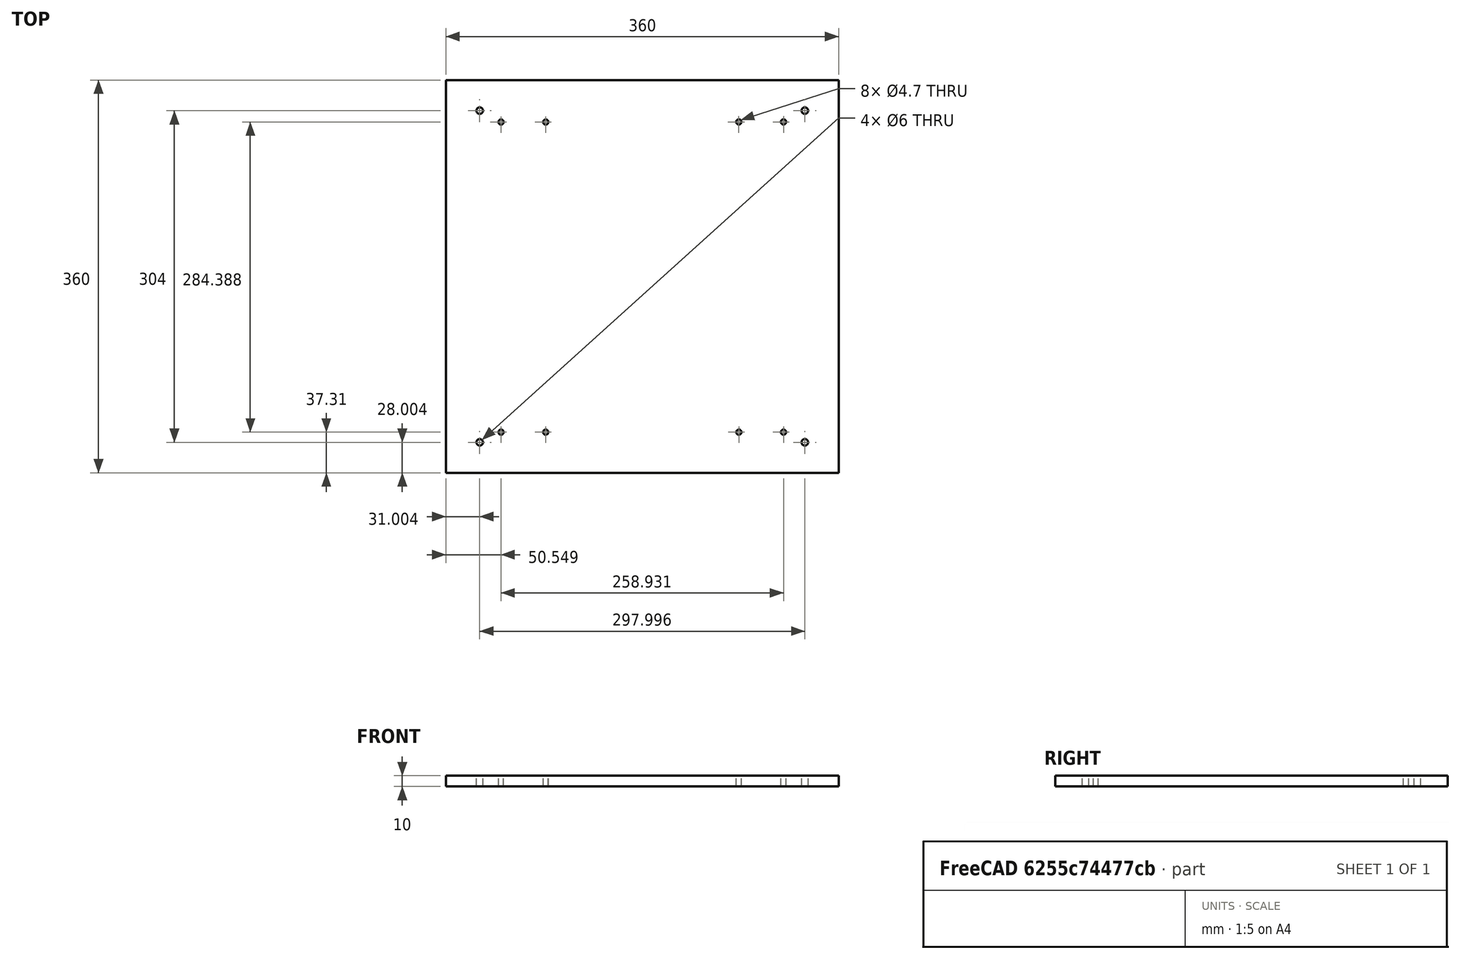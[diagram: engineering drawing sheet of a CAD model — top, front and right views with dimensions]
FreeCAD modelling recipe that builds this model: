
FCSTD DOCUMENT  (FreeCAD 0.14R3702 (Git))
Label: bed
License: CC-BY 3.0
LicenseURL: http://creativecommons.org/licenses/by/3.0/
objects: Part::Cylinder×12, Part::Cut×12, Part::Box×1
note: 25 computed .brp shape members not serialized (recipe doc carries the construction recipe); baked Part::Feature solids carry a one-line shape summary decoded from their .brp

FEATURE [Part::Box] Box  label="Cube"
  Height = 10
  Length = 360
  Placement = pos=(795.334,70.8936,98.54) rot=(0,0,1;0rad)
  Width = 360
FEATURE [Part::Cylinder] Cylinder
  Angle = 360
  Height = 100
  Placement = pos=(845.879,108.2,42.0127) rot=(0,0,1;0rad)
  Radius = 2.35
FEATURE [Part::Cylinder] Cylinder001
  Angle = 360
  Height = 100
  Placement = pos=(886.821,108.2,42.0127) rot=(0,0,1;0rad)
  Radius = 2.35
FEATURE [Part::Cylinder] Cylinder002
  Angle = 360
  Height = 100
  Placement = pos=(1063.88,108.2,42.0127) rot=(0,0,1;0rad)
  Radius = 2.35
FEATURE [Part::Cylinder] Cylinder003
  Angle = 360
  Height = 100
  Placement = pos=(1104.81,108.2,42.0127) rot=(0,0,1;0rad)
  Radius = 2.35
FEATURE [Part::Cylinder] Cylinder004
  Angle = 360
  Height = 100
  Placement = pos=(845.879,392.51,42.0127) rot=(0,0,1;0rad)
  Radius = 2.35
FEATURE [Part::Cylinder] Cylinder005
  Angle = 360
  Height = 100
  Placement = pos=(886.877,392.51,42.0127) rot=(0,0,1;0rad)
  Radius = 2.35
FEATURE [Part::Cylinder] Cylinder006
  Angle = 360
  Height = 100
  Placement = pos=(1063.81,392.588,42.0128) rot=(0,0,1;0rad)
  Radius = 2.35
FEATURE [Part::Cylinder] Cylinder007
  Angle = 360
  Height = 100
  Placement = pos=(1104.81,392.584,42.0127) rot=(0,0,1;0rad)
  Radius = 2.35
FEATURE [Part::Cut] Cut
  Base = -> Box
  Tool = -> Cylinder
FEATURE [Part::Cut] Cut001
  Base = -> Cut
  Tool = -> Cylinder001
FEATURE [Part::Cut] Cut002
  Base = -> Cut001
  Tool = -> Cylinder002
FEATURE [Part::Cut] Cut003
  Base = -> Cut002
  Tool = -> Cylinder003
FEATURE [Part::Cut] Cut004
  Base = -> Cut003
  Tool = -> Cylinder004
FEATURE [Part::Cut] Cut005
  Base = -> Cut004
  Tool = -> Cylinder005
FEATURE [Part::Cut] Cut006
  Base = -> Cut005
  Tool = -> Cylinder006
FEATURE [Part::Cut] Cut007
  Base = -> Cut006
  Tool = -> Cylinder007
FEATURE [Part::Cylinder] Cylinder008
  Angle = 360
  Height = 80
  Placement = pos=(826.334,98.8936,72.563) rot=(0,0,1;0rad)
  Radius = 3
FEATURE [Part::Cylinder] Cylinder009
  Angle = 360
  Height = 80
  Placement = pos=(1124.33,98.8936,72.563) rot=(0,0,1;0rad)
  Radius = 3
FEATURE [Part::Cylinder] Cylinder010
  Angle = 360
  Height = 80
  Placement = pos=(826.334,402.894,72.563) rot=(0,0,1;0rad)
  Radius = 3
FEATURE [Part::Cylinder] Cylinder011
  Angle = 360
  Height = 80
  Placement = pos=(1124.33,402.894,72.563) rot=(0,0,1;0rad)
  Radius = 3
FEATURE [Part::Cut] Cut008
  Base = -> Cut007
  Tool = -> Cylinder008
FEATURE [Part::Cut] Cut009
  Base = -> Cut008
  Tool = -> Cylinder009
FEATURE [Part::Cut] Cut010
  Base = -> Cut009
  Tool = -> Cylinder010
FEATURE [Part::Cut] Cut011
  Base = -> Cut010
  Tool = -> Cylinder011
